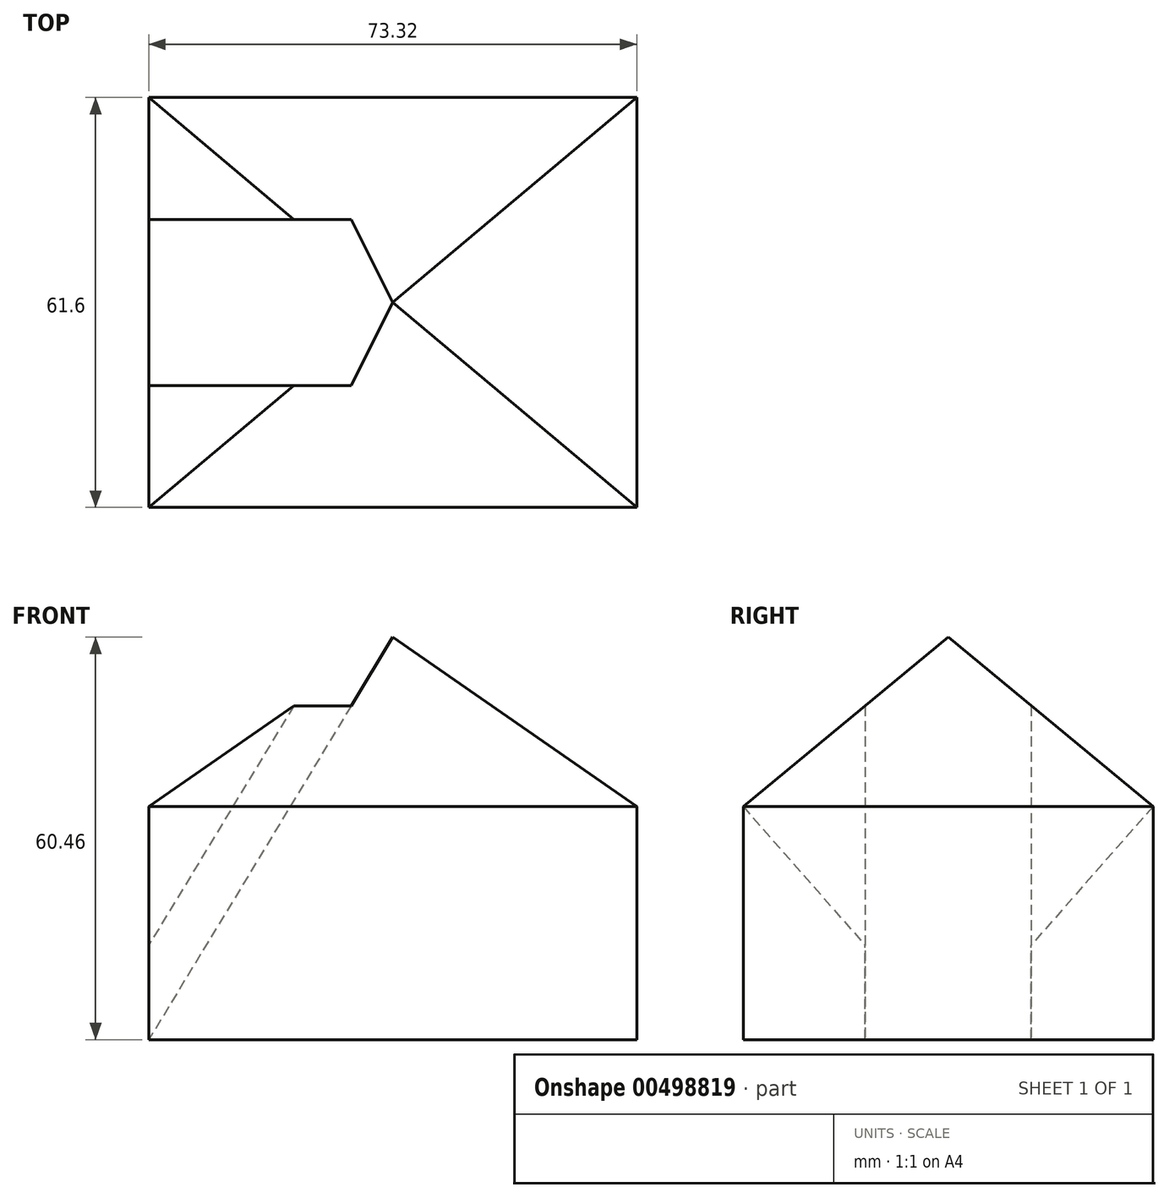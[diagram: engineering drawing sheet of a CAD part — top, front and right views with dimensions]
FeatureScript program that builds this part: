
annotation { "Feature Type Name" : "Feature", "Feature Type Description" : "" }
export const myFeature = defineFeature(function(context is Context, id is Id, definition is map)
    precondition{}
    {
        {
            var Q0;
            Q0=qCreatedBy(makeId("Front.planeOp"),FACE);
            var sketch = newSketch(context, id + "F0", { "sketchPlane" : qUnion([Q0])});
            skLineSegment(sketch, "E0.bottom", {"start": v(36.66, 30.23) * mm, "end": v(-36.66, 30.23) * mm});
            skLineSegment(sketch, "E0.top", {"start": v(36.66, -30.23) * mm, "end": v(-36.66, -30.23) * mm});
            skLineSegment(sketch, "E0.left", {"start": v(36.66, 30.23) * mm, "end": v(36.66, -30.23) * mm});
            skLineSegment(sketch, "E0.right", {"start": v(-36.66, 30.23) * mm, "end": v(-36.66, -30.23) * mm});
            skPoint(sketch, "E0.middle", {"position": v(0, 0) * mm});
            skSolve(sketch);
        }
        {
            var Q0;
            Q0=makeQuery(id+"F0.imprint","IMPRINT",FACE,{"disambiguationData":[TD([[makeQuery(id+"F0.imprint","IMPRINT",EDGE,{"derivedFrom":sQuery(id+"F0.wireOp",EDGE,"E0.bottom")}),1.0]])]});
            extrude(context, id + "F1", {"entities" : qUnion([Q0]), "endBound" : BoundingType.SYMMETRIC, "depth" : 61.6 * mm});
        }
        {
            var Q0;
            Q0=makeQuery(id+"F1.opExtrude","CAP_FACE",FACE,{"disambiguationData":[OSD([sQuery(id+"F0.wireOp",EDGE,"E0.bottom"),sQuery(id+"F0.wireOp",EDGE,"E0.top"),sQuery(id+"F0.wireOp",EDGE,"E0.left"),sQuery(id+"F0.wireOp",EDGE,"E0.right")])],"isStart":false});
            var sketch = newSketch(context, id + "F2", { "sketchPlane" : qUnion([Q0])});
            skLineSegment(sketch, "E1", {"start": v(-36.66, 4.8) * mm, "end": v(0, 30.23) * mm});
            skLineSegment(sketch, "E2", {"start": v(0, 30.23) * mm, "end": v(36.66, 4.8) * mm});
            skLineSegment(sketch, "E3", {"start": v(36.66, 4.8) * mm, "end": v(36.66, 30.23) * mm});
            skLineSegment(sketch, "E4", {"start": v(36.66, 30.23) * mm, "end": v(-36.66, 30.23) * mm});
            skLineSegment(sketch, "E5", {"start": v(-36.66, 30.23) * mm, "end": v(-36.66, 4.8) * mm});
            skSolve(sketch);
        }
        {
            var Q0;
            {var subQ0=sQuery(id+"F2.wireOp",EDGE,"E1");Q0=makeQuery(id+"F2.imprint","IMPRINT",FACE,{"disambiguationData":[TD([[makeQuery(id+"F2.imprint","IMPRINT",EDGE,{"derivedFrom":subQ0}),1.0]])]});}
            var Q1;
            {var subQ0=sQuery(id+"F2.wireOp",EDGE,"E2");Q1=makeQuery(id+"F2.imprint","IMPRINT",FACE,{"disambiguationData":[TD([[makeQuery(id+"F2.imprint","IMPRINT",EDGE,{"derivedFrom":subQ0}),1.0]])]});}
            extrude(context, id + "F3", {"entities" : qUnion([Q0, Q1]), "operationType" : NewBodyOperationType.REMOVE, "endBound" : BoundingType.THROUGH_ALL, "oppositeDirection" : true, "depth" : 25 * mm});
        }
        {
            var Q0;
            Q0=makeQuery(id+"F1.opExtrude","SWEPT_FACE",FACE,{"disambiguationData":[OSD([sQuery(id+"F0.wireOp",EDGE,"E0.right")])]});
            var sketch = newSketch(context, id + "F4", { "sketchPlane" : qUnion([Q0])});
            skLineSegment(sketch, "E6.0", {"start": v(-30.8, 30.23) * mm, "end": v(30.8, 30.23) * mm});
            skLineSegment(sketch, "E7.0", {"start": v(-30.8, 4.8) * mm, "end": v(-30.8, 30.23) * mm});
            skLineSegment(sketch, "E8.0", {"start": v(30.8, 4.8) * mm, "end": v(30.8, 30.23) * mm});
            skLineSegment(sketch, "E9", {"start": v(-30.8, 4.8) * mm, "end": v(0, 30.23) * mm});
            skLineSegment(sketch, "E10", {"start": v(0, 30.23) * mm, "end": v(30.8, 4.8) * mm});
            skSolve(sketch);
        }
        {
            var Q0;
            {var subQ0=sQuery(id+"F4.wireOp",EDGE,"E7.0");Q0=makeQuery(id+"F4.imprint","IMPRINT",FACE,{"disambiguationData":[TD([[makeQuery(id+"F4.imprint","IMPRINT",EDGE,{"derivedFrom":subQ0}),-1.0]])]});}
            var Q1;
            {var subQ0=sQuery(id+"F4.wireOp",EDGE,"E8.0");Q1=makeQuery(id+"F4.imprint","IMPRINT",FACE,{"disambiguationData":[TD([[makeQuery(id+"F4.imprint","IMPRINT",EDGE,{"derivedFrom":subQ0}),1.0]])]});}
            var Q2;
            Q2=sQuery(id+"F4.wireOp",EDGE,"E7.0");
            extrude(context, id + "F5", {"entities" : qUnion([Q0, Q1]), "operationType" : NewBodyOperationType.REMOVE, "surfaceEntities" : qUnion([Q2]), "endBound" : BoundingType.THROUGH_ALL, "oppositeDirection" : true, "depth" : 25 * mm});
        }
        {
            var Q0;
            Q0=qCreatedBy(makeId("Front.planeOp"),FACE);
            var sketch = newSketch(context, id + "F6", { "sketchPlane" : qUnion([Q0])});
            skPoint(sketch, "E11.0", {"position": v(0, 30.23) * mm});
            skLineSegment(sketch, "E12", {"start": v(-36.66, -30.23) * mm, "end": v(-36.66, 4.8) * mm});
            skLineSegment(sketch, "E13", {"start": v(0, 30.23) * mm, "end": v(-36.66, 4.8) * mm});
            skLineSegment(sketch, "E14", {"start": v(0, 30.23) * mm, "end": v(-36.66, -30.23) * mm});
            skSolve(sketch);
        }
        {
            var Q0;
            Q0=makeQuery(id+"F1.opExtrude","SWEPT_EDGE",EDGE,{"disambiguationData":[OSD([sQuery(id+"F0.wireOp",EDGE,"E0.top"),sQuery(id+"F0.wireOp",EDGE,"E0.right")])]});
            cPoint(context, id + "F7", {"entities" : qUnion([Q0]), "parameter" : 0.5});
        }
        {
            var Q0;
            Q0 = qCreatedBy(id + "F7" ,VERTEX);
            var Q1;
            Q1=sQuery(id+"F6.wireOp",VERTEX,"E11.0");
            var Q2;
            {var subQ0=sQuery(id+"F2.wireOp",EDGE,"E5");var subQ1=sQuery(id+"F2.wireOp",EDGE,"E1");var subQ2=sQuery(id+"F0.wireOp",EDGE,"E0.right");Q2=makeQuery(id+"F5.boolean.opBoolean","MERGE",VERTEX,{"derivedFrom":[makeQuery(id+"F3.boolean.opBoolean","COPY",VERTEX,{"derivedFrom":makeQuery(id+"F3.opExtrude","CAP_VERTEX",VERTEX,{"disambiguationData":[OSD([subQ2,subQ1,subQ0])],"isStart":true})}),makeQuery(id+"F5.opExtrude","CAP_VERTEX",VERTEX,{"disambiguationData":[OSD([subQ2,subQ1,subQ0,sQuery(id+"F4.wireOp",EDGE,"E8.0"),sQuery(id+"F4.wireOp",EDGE,"E10")])],"isStart":true})]});}
            cPlane(context, id + "F8", {"entities" : qUnion([Q0, Q1, Q2]), "cplaneType" : CPlaneType.THREE_POINT, "offset" : 25 * mm, "width" : 150 * mm, "height" : 150 * mm});
        }
        {
            var Q0;
            Q0=qCreatedBy(id+"F8.planeOp",FACE);
            var sketch = newSketch(context, id + "F9", { "sketchPlane" : qUnion([Q0])});
            skLineSegment(sketch, "E15.0", {"start": v(7.96, 25.85) * mm, "end": v(7.96, -44.86) * mm, "construction": true});
            skLineSegment(sketch, "E16.0", {"start": v(43.72, -14.9) * mm, "end": v(7.96, 25.85) * mm, "construction": true});
            skLineSegment(sketch, "E17.0", {"start": v(43.72, -14.9) * mm, "end": v(34.5, -44.86) * mm, "construction": true});
            skLineSegment(sketch, "E18", {"start": v(7.96, -9.5) * mm, "end": v(43.72, -14.9) * mm});
            skSolve(sketch);
        }
        {
            var Q0;
            Q0 = qSketchRegion(id + "F6", true);
            var Q1;
            Q1=sQuery(id+"F9.wireOp",EDGE,"E18");
            sweep(context, id + "F10", {"operationType" : NewBodyOperationType.REMOVE, "profiles" : qUnion([Q0]), "path" : qUnion([Q1])});
        }
        {
            var Q0;
            Q0=makeQuery(id+"F1.opExtrude","SWEPT_BODY",BODY,{"disambiguationData":[OSD([sQuery(id+"F0.wireOp",EDGE,"E0.bottom"),sQuery(id+"F0.wireOp",EDGE,"E0.top"),sQuery(id+"F0.wireOp",EDGE,"E0.left"),sQuery(id+"F0.wireOp",EDGE,"E0.right")])]});
            var Q1;
            Q1=qCreatedBy(makeId("Front.planeOp"),FACE);
            mirror(context, id + "F11", {"operationType" : NewBodyOperationType.INTERSECT, "entities" : qUnion([Q0]), "mirrorPlane" : qUnion([Q1])});
        }
        {
            var Q0;
            Q0 = qSketchRegion(id + "F6", true);
            var Q1;
            Q1=sQuery(id+"F6.wireOp",EDGE,"E14");
            var Q2;
            Q2=sQuery(id+"F6.wireOp",EDGE,"E12");
            var Q3;
            Q3=sQuery(id+"F6.wireOp",EDGE,"E13");
            extrude(context, id + "F12", {"entities" : qUnion([Q0]), "operationType" : NewBodyOperationType.REMOVE, "surfaceEntities" : qUnion([Q1, Q2, Q3]), "endBound" : BoundingType.SYMMETRIC, "oppositeDirection" : true, "depth" : 25 * mm});
        }
    });
